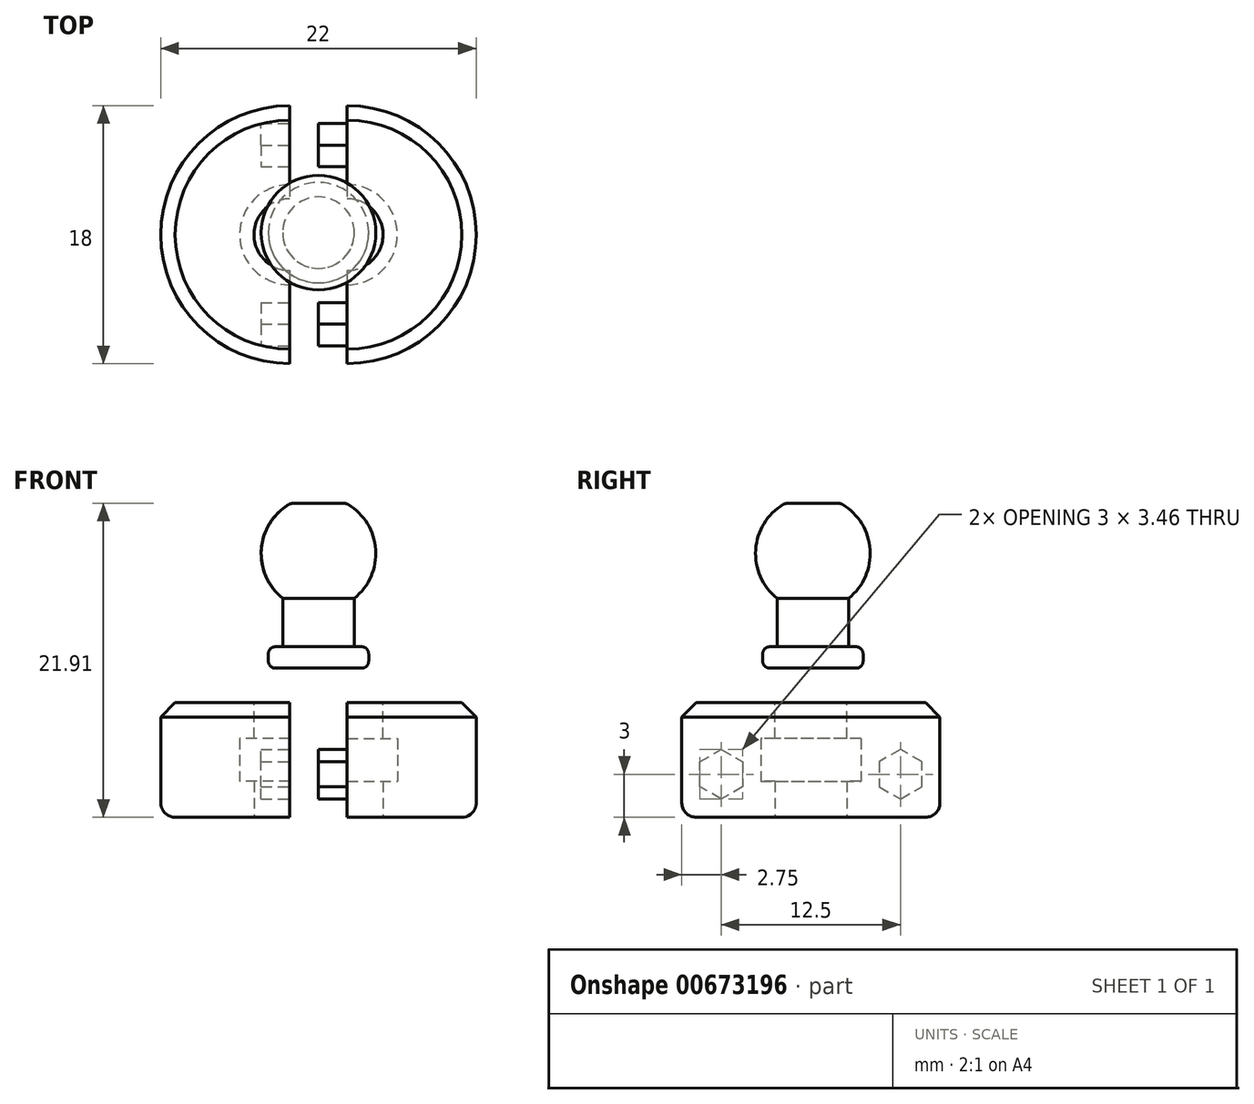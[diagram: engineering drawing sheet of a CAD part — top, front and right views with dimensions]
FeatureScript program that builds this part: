
annotation { "Feature Type Name" : "Feature", "Feature Type Description" : "" }
export const myFeature = defineFeature(function(context is Context, id is Id, definition is map)
    precondition{}
    {
        {
            var Q0;
            Q0=qCreatedBy(makeId("Right.planeOp"),FACE);
            var sketch = newSketch(context, id + "F0", { "sketchPlane" : qUnion([Q0])});
            skLineSegment(sketch, "E0.bottom", {"start": v(0, 0) * mm, "end": v(-18, 0) * mm});
            skLineSegment(sketch, "E0.top", {"start": v(0, 8) * mm, "end": v(-18, 8) * mm});
            skLineSegment(sketch, "E0.left", {"start": v(0, 0) * mm, "end": v(0, 8) * mm});
            skLineSegment(sketch, "E0.right", {"start": v(-18, 0) * mm, "end": v(-18, 8) * mm});
            skSolve(sketch);
        }
        {
            var Q0;
            Q0=makeQuery(id+"F0.imprint","IMPRINT",FACE,{"disambiguationData":[TD([[makeQuery(id+"F0.imprint","IMPRINT",EDGE,{"derivedFrom":sQuery(id+"F0.wireOp",EDGE,"E0.bottom")}),-1.0]])]});
            extrude(context, id + "F1", {"entities" : qUnion([Q0]), "depth" : 9 * mm});
        }
        {
            var Q0;
            Q0=makeQuery(id+"F1.opExtrude","SWEPT_FACE",FACE,{"disambiguationData":[OSD([sQuery(id+"F0.wireOp",EDGE,"E0.bottom")])]});
            var sketch = newSketch(context, id + "F2", { "sketchPlane" : qUnion([Q0])});
            skArc(sketch, "E1", {"start": v(9, 11.5) * mm, "mid": v(6.5, 9) * mm, "end": v(9, 6.5) * mm});
            skArc(sketch, "E2", {"start": v(9, 12.5) * mm, "mid": v(5.5, 9) * mm, "end": v(9, 5.5) * mm});
            skLineSegment(sketch, "E3", {"start": v(9, 12.5) * mm, "end": v(9, 5.5) * mm});
            skSolve(sketch);
        }
        {
            var Q0;
            Q0=qSketchRegion(id+"F2",true);
            extrude(context, id + "F3", {"entities" : qUnion([Q0]), "operationType" : NewBodyOperationType.REMOVE, "oppositeDirection" : true, "depth" : 4 * mm});
        }
        {
            var Q0;
            {var subQ0=sQuery(id+"F2.wireOp",EDGE,"E1");Q0=makeQuery(id+"F2.imprint","IMPRINT",FACE,{"disambiguationData":[TD([[makeQuery(id+"F2.imprint","IMPRINT",EDGE,{"derivedFrom":subQ0}),-1.0]])]});}
            extrude(context, id + "F4", {"entities" : qUnion([Q0]), "operationType" : NewBodyOperationType.ADD, "oppositeDirection" : true, "depth" : 2.5 * mm});
        }
        {
            var Q0;
            {var subQ0=sQuery(id+"F2.wireOp",EDGE,"E3");var subQ1=sQuery(id+"F2.wireOp",EDGE,"E1");var subQ3=sQuery(id+"F0.wireOp",EDGE,"E0.bottom");Q0=makeQuery(id+"F4.boolean.opBoolean","MERGE",FACE,{"derivedFrom":[makeQuery(id+"F1.opExtrude","CAP_FACE",FACE,{"disambiguationData":[OSD([subQ3,sQuery(id+"F0.wireOp",EDGE,"E0.top"),sQuery(id+"F0.wireOp",EDGE,"E0.left"),sQuery(id+"F0.wireOp",EDGE,"E0.right")])],"isStart":false}),makeQuery(id+"F4.opExtrude","SWEPT_FACE",FACE,{"disambiguationData":[OSD([subQ0]),TDD([makeQuery(id+"F2.imprint","IMPRINT",EDGE,{"disambiguationData":[TD([[makeQuery(id+"F2.imprint","INTERSECT",VERTEX,{"disambiguationData":[OD(1.0)],"derivedFrom":[subQ1,subQ0]}),1.0]])],"derivedFrom":subQ0})])]}),makeQuery(id+"F4.opExtrude","SWEPT_FACE",FACE,{"disambiguationData":[OSD([subQ0]),TDD([makeQuery(id+"F2.imprint","IMPRINT",EDGE,{"disambiguationData":[TD([[makeQuery(id+"F2.imprint","INTERSECT",VERTEX,{"disambiguationData":[OD(0.0)],"derivedFrom":[subQ1,subQ0]}),-1.0]])],"derivedFrom":subQ0})])]})]});}
            var sketch = newSketch(context, id + "F5", { "sketchPlane" : qUnion([Q0])});
            skSolve(sketch);
        }
        {
            var Q0;
            Q0=makeQuery(id+"F1.opExtrude","CAP_EDGE",EDGE,{"disambiguationData":[OSD([sQuery(id+"F0.wireOp",EDGE,"E0.right")])],"isStart":true});
            var Q1;
            Q1=makeQuery(id+"F1.opExtrude","CAP_EDGE",EDGE,{"disambiguationData":[OSD([sQuery(id+"F0.wireOp",EDGE,"E0.left")])],"isStart":true});
            fillet(context, id + "F6", {"entities" : qUnion([Q0, Q1]), "radius" : 9 * mm, "tangentPropagation" : true, "allowEdgeOverflow" : false});
        }
        {
            var Q0;
            {var subQ12=sQuery(id+"F0.wireOp",EDGE,"E0.top");Q0=makeQuery(id+"F5.imprint","IMPRINT",FACE,{"disambiguationData":[TD([[makeQuery(id+"F5.imprint","IMPRINT",EDGE,{"derivedFrom":makeQuery(id+"F1.opExtrude","CAP_EDGE",EDGE,{"disambiguationData":[OSD([subQ12])],"isStart":false})}),1.0]])]});}
            var sketch = newSketch(context, id + "F7", { "sketchPlane" : qUnion([Q0])});
            skLineSegment(sketch, "E4", {"start": v(0, 0) * mm, "end": v(-18, 0) * mm, "construction": true});
            skLineSegment(sketch, "E5", {"start": v(-9, 0) * mm, "end": v(-9, 6) * mm, "construction": true});
            skLineSegment(sketch, "E6", {"start": v(-9, 6) * mm, "end": v(-12.5, 6) * mm, "construction": true});
            skLineSegment(sketch, "E7.bottom", {"start": v(-12.5, 6) * mm, "end": v(-18, 6) * mm, "construction": true});
            skLineSegment(sketch, "E7.top", {"start": v(-12.5, 0) * mm, "end": v(-18, 0) * mm, "construction": true});
            skLineSegment(sketch, "E7.left", {"start": v(-12.5, 6) * mm, "end": v(-12.5, 0) * mm, "construction": true});
            skLineSegment(sketch, "E7.right", {"start": v(-18, 6) * mm, "end": v(-18, 0) * mm, "construction": true});
            skCircle(sketch, "E8.cCircle", {"center": v(-15.25, 3) * mm, "radius": 1.5 * mm});
            skPoint(sketch, "E8.cCircle.centerSnap0", {"position": v(-18, 3) * mm});
            skPoint(sketch, "E8.cCircle.centerSnap1", {"position": v(-15.25, 6) * mm});
            skLineSegment(sketch, "E8.0", {"start": v(-16.75, 2.13) * mm, "end": v(-16.75, 3.87) * mm});
            skLineSegment(sketch, "E8.1", {"start": v(-16.75, 3.87) * mm, "end": v(-15.25, 4.73) * mm});
            skLineSegment(sketch, "E8.2", {"start": v(-15.25, 4.73) * mm, "end": v(-13.75, 3.87) * mm});
            skLineSegment(sketch, "E8.3", {"start": v(-13.75, 3.87) * mm, "end": v(-13.75, 2.13) * mm});
            skLineSegment(sketch, "E8.4", {"start": v(-13.75, 2.13) * mm, "end": v(-15.25, 1.27) * mm});
            skLineSegment(sketch, "E8.5", {"start": v(-15.25, 1.27) * mm, "end": v(-16.75, 2.13) * mm});
            skPoint(sketch, "E8.0.midPoint", {"position": v(-16.75, 3) * mm});
            skLineSegment(sketch, "E9.MirrorCS", {"start": v(-2.75, 1.27) * mm, "end": v(-1.25, 2.13) * mm});
            skPoint(sketch, "E10.MirrorP", {"position": v(-1.25, 3) * mm});
            skLineSegment(sketch, "E11.MirrorCS", {"start": v(-4.25, 2.13) * mm, "end": v(-2.75, 1.27) * mm});
            skLineSegment(sketch, "E12.MirrorCS", {"start": v(-4.25, 3.87) * mm, "end": v(-4.25, 2.13) * mm});
            skLineSegment(sketch, "E13.MirrorCS", {"start": v(-2.75, 4.73) * mm, "end": v(-4.25, 3.87) * mm});
            skLineSegment(sketch, "E14.MirrorCS", {"start": v(-1.25, 2.13) * mm, "end": v(-1.25, 3.87) * mm});
            skLineSegment(sketch, "E15.MirrorCS", {"start": v(-1.25, 3.87) * mm, "end": v(-2.75, 4.73) * mm});
            skCircle(sketch, "E16.MirrorC", {"center": v(-2.75, 3) * mm, "radius": 1.5 * mm});
            skSolve(sketch);
        }
        {
            var Q0;
            Q0=qSketchRegion(id+"F7",true);
            extrude(context, id + "F8", {"entities" : qUnion([Q0]), "operationType" : NewBodyOperationType.REMOVE, "oppositeDirection" : true, "depth" : 2 * mm});
        }
        {
            var Q0;
            Q0=makeQuery(id+"F1.opExtrude","SWEPT_FACE",FACE,{"disambiguationData":[OSD([sQuery(id+"F0.wireOp",EDGE,"E0.top")])]});
            var sketch = newSketch(context, id + "F9", { "sketchPlane" : qUnion([Q0])});
            skArc(sketch, "E17", {"start": v(9, -6.5) * mm, "mid": v(6.5, -9) * mm, "end": v(9, -11.5) * mm});
            skArc(sketch, "E18", {"start": v(9, -5.5) * mm, "mid": v(5.5, -9) * mm, "end": v(9, -12.5) * mm});
            skLineSegment(sketch, "E19", {"start": v(9, -12.5) * mm, "end": v(9, -5.5) * mm});
            skSolve(sketch);
        }
        {
            var Q0;
            Q0=qSketchRegion(id+"F9",true);
            extrude(context, id + "F10", {"entities" : qUnion([Q0]), "operationType" : NewBodyOperationType.REMOVE, "oppositeDirection" : true, "depth" : 4 * mm});
        }
        {
            var Q0;
            {var subQ0=sQuery(id+"F9.wireOp",EDGE,"E17");Q0=makeQuery(id+"F9.imprint","IMPRINT",FACE,{"disambiguationData":[TD([[makeQuery(id+"F9.imprint","IMPRINT",EDGE,{"derivedFrom":subQ0}),-1.0]])]});}
            extrude(context, id + "F11", {"entities" : qUnion([Q0]), "operationType" : NewBodyOperationType.ADD, "oppositeDirection" : true, "depth" : 2.5 * mm});
        }
        {
            var Q0;
            Q0=qCreatedBy(makeId("Right.planeOp"),FACE);
            cPlane(context, id + "F12", {"entities" : qUnion([Q0]), "cplaneType" : CPlaneType.OFFSET, "offset" : 11 * mm, "width" : 150 * mm, "height" : 150 * mm});
        }
        {
            var Q0;
            Q0=qCreatedBy(id+"F12.planeOp",FACE);
            var sketch = newSketch(context, id + "F13", { "sketchPlane" : qUnion([Q0])});
            skLineSegment(sketch, "E20", {"start": v(-8.86, 10.4) * mm, "end": v(-8.86, 18.4) * mm, "construction": true});
            skLineSegment(sketch, "E21", {"start": v(-8.86, 10.4) * mm, "end": v(-12.36, 10.4) * mm});
            skLineSegment(sketch, "E22", {"start": v(-12.36, 10.4) * mm, "end": v(-12.36, 11.9) * mm});
            skLineSegment(sketch, "E23", {"start": v(-12.36, 11.9) * mm, "end": v(-11.36, 11.9) * mm});
            skLineSegment(sketch, "E24", {"start": v(-11.36, 11.9) * mm, "end": v(-11.36, 14.4) * mm});
            skLineSegment(sketch, "E25", {"start": v(-11.36, 14.4) * mm, "end": v(-8.86, 14.4) * mm, "construction": true});
            skArc(sketch, "E26", {"start": v(-10.8, 21.9) * mm, "mid": v(-12.85, 18.74) * mm, "end": v(-11.36, 15.28) * mm});
            skLineSegment(sketch, "E27", {"start": v(-11.36, 14.4) * mm, "end": v(-11.36, 15.28) * mm});
            skLineSegment(sketch, "E28", {"start": v(-8.86, 18.4) * mm, "end": v(-8.86, 22.4) * mm, "construction": true});
            skLineSegment(sketch, "E29", {"start": v(-8.86, 22.4) * mm, "end": v(-8.86, 21.9) * mm, "construction": true});
            skLineSegment(sketch, "E30", {"start": v(-8.86, 21.9) * mm, "end": v(-10.8, 21.9) * mm});
            skLineSegment(sketch, "E31", {"start": v(-8.86, 21.9) * mm, "end": v(-8.86, 10.4) * mm});
            skSolve(sketch);
        }
        {
            var Q0;
            Q0=qSketchRegion(id+"F13",true);
            var Q1;
            Q1=sQuery(id+"F13.wireOp",EDGE,"E31");
            revolve(context, id + "F14", {"entities" : qUnion([Q0]), "axis" : qUnion([Q1]), "revolveType" : RevolveType.FULL});
        }
        {
            var Q0;
            Q0=makeQuery(id+"F14.opRevolve","SWEPT_FACE",FACE,{"disambiguationData":[OSD([sQuery(id+"F13.wireOp",EDGE,"E22")])]});
            var Q1;
            Q1=makeQuery(id+"F14.opRevolve","SWEPT_EDGE",EDGE,{"disambiguationData":[OSD([sQuery(id+"F13.wireOp",EDGE,"E26"),sQuery(id+"F13.wireOp",EDGE,"E30")])]});
            fillet(context, id + "F15", {"entities" : qUnion([Q0, Q1]), "radius" : .5 * mm, "tangentPropagation" : true, "allowEdgeOverflow" : false});
        }
        {
            var Q0;
            Q0=makeQuery(id+"F1.opExtrude","SWEPT_BODY",BODY,{"disambiguationData":[OSD([sQuery(id+"F0.wireOp",EDGE,"E0.bottom"),sQuery(id+"F0.wireOp",EDGE,"E0.top"),sQuery(id+"F0.wireOp",EDGE,"E0.left"),sQuery(id+"F0.wireOp",EDGE,"E0.right")])]});
            var Q1;
            Q1=qCreatedBy(id+"F12.planeOp",FACE);
            mirror(context, id + "F16", {"entities" : qUnion([Q0]), "mirrorPlane" : qUnion([Q1])});
        }
        {
            var Q0;
            Q0=makeQuery(id+"F16.opPattern","COPY",FACE,{"derivedFrom":makeQuery(id+"F8.boolean.opBoolean","COPY",FACE,{"derivedFrom":makeQuery(id+"F8.opExtrude","CAP_FACE",FACE,{"disambiguationData":[OSD([sQuery(id+"F7.wireOp",EDGE,"E8.0"),sQuery(id+"F7.wireOp",EDGE,"E8.1"),sQuery(id+"F7.wireOp",EDGE,"E8.2"),sQuery(id+"F7.wireOp",EDGE,"E8.3"),sQuery(id+"F7.wireOp",EDGE,"E8.4"),sQuery(id+"F7.wireOp",EDGE,"E8.5")])],"isStart":false})}),"instanceName":"1"});
            var Q1;
            Q1=makeQuery(id+"F16.opPattern","COPY",FACE,{"derivedFrom":makeQuery(id+"F8.boolean.opBoolean","COPY",FACE,{"derivedFrom":makeQuery(id+"F8.opExtrude","CAP_FACE",FACE,{"disambiguationData":[OSD([sQuery(id+"F7.wireOp",EDGE,"E9.MirrorCS"),sQuery(id+"F7.wireOp",EDGE,"E11.MirrorCS"),sQuery(id+"F7.wireOp",EDGE,"E12.MirrorCS"),sQuery(id+"F7.wireOp",EDGE,"E13.MirrorCS"),sQuery(id+"F7.wireOp",EDGE,"E14.MirrorCS"),sQuery(id+"F7.wireOp",EDGE,"E15.MirrorCS")])],"isStart":false})}),"instanceName":"1"});
            extrude(context, id + "F17", {"entities" : qUnion([Q0, Q1]), "operationType" : NewBodyOperationType.ADD, "depth" : 4 * mm});
        }
        {
            var Q0;
            Q0=makeQuery(id+"F6.opFillet","BLEND_EDGE",EDGE,{"blendedFrom":[makeQuery(id+"F1.opExtrude","CAP_EDGE",EDGE,{"disambiguationData":[OSD([sQuery(id+"F0.wireOp",EDGE,"E0.left")])],"isStart":true}),makeQuery(id+"F4.boolean.opBoolean","MERGE",FACE,{"derivedFrom":[makeQuery(id+"F1.opExtrude","SWEPT_FACE",FACE,{"disambiguationData":[OSD([sQuery(id+"F0.wireOp",EDGE,"E0.bottom")])]}),makeQuery(id+"F4.opExtrude","CAP_FACE",FACE,{"disambiguationData":[OSD([sQuery(id+"F2.wireOp",EDGE,"E1"),sQuery(id+"F2.wireOp",EDGE,"E2"),sQuery(id+"F2.wireOp",EDGE,"E3")])],"isStart":true})]})],"blendedInto":[makeQuery(id+"F4.boolean.opBoolean","MERGE",FACE,{"derivedFrom":[makeQuery(id+"F1.opExtrude","SWEPT_FACE",FACE,{"disambiguationData":[OSD([sQuery(id+"F0.wireOp",EDGE,"E0.bottom")])]}),makeQuery(id+"F4.opExtrude","CAP_FACE",FACE,{"disambiguationData":[OSD([sQuery(id+"F2.wireOp",EDGE,"E1"),sQuery(id+"F2.wireOp",EDGE,"E2"),sQuery(id+"F2.wireOp",EDGE,"E3")])],"isStart":true})]})]});
            var Q1;
            Q1=makeQuery(id+"F16.opPattern","COPY",EDGE,{"derivedFrom":makeQuery(id+"F6.opFillet","BLEND_EDGE",EDGE,{"blendedFrom":[makeQuery(id+"F1.opExtrude","CAP_EDGE",EDGE,{"disambiguationData":[OSD([sQuery(id+"F0.wireOp",EDGE,"E0.left")])],"isStart":true}),makeQuery(id+"F4.boolean.opBoolean","MERGE",FACE,{"derivedFrom":[makeQuery(id+"F1.opExtrude","SWEPT_FACE",FACE,{"disambiguationData":[OSD([sQuery(id+"F0.wireOp",EDGE,"E0.bottom")])]}),makeQuery(id+"F4.opExtrude","CAP_FACE",FACE,{"disambiguationData":[OSD([sQuery(id+"F2.wireOp",EDGE,"E1"),sQuery(id+"F2.wireOp",EDGE,"E2"),sQuery(id+"F2.wireOp",EDGE,"E3")])],"isStart":true})]})],"blendedInto":[makeQuery(id+"F4.boolean.opBoolean","MERGE",FACE,{"derivedFrom":[makeQuery(id+"F1.opExtrude","SWEPT_FACE",FACE,{"disambiguationData":[OSD([sQuery(id+"F0.wireOp",EDGE,"E0.bottom")])]}),makeQuery(id+"F4.opExtrude","CAP_FACE",FACE,{"disambiguationData":[OSD([sQuery(id+"F2.wireOp",EDGE,"E1"),sQuery(id+"F2.wireOp",EDGE,"E2"),sQuery(id+"F2.wireOp",EDGE,"E3")])],"isStart":true})]})]}),"instanceName":"1"});
            fillet(context, id + "F18", {"entities" : qUnion([Q0, Q1]), "radius" : 1 * mm, "tangentPropagation" : true, "allowEdgeOverflow" : false});
        }
        {
            var Q0;
            Q0=makeQuery(id+"F6.opFillet","BLEND_EDGE",EDGE,{"blendedFrom":[makeQuery(id+"F1.opExtrude","CAP_EDGE",EDGE,{"disambiguationData":[OSD([sQuery(id+"F0.wireOp",EDGE,"E0.left")])],"isStart":true}),makeQuery(id+"F1.opExtrude","SWEPT_FACE",FACE,{"disambiguationData":[OSD([sQuery(id+"F0.wireOp",EDGE,"E0.top")])]})],"blendedInto":[makeQuery(id+"F1.opExtrude","SWEPT_FACE",FACE,{"disambiguationData":[OSD([sQuery(id+"F0.wireOp",EDGE,"E0.top")])]})]});
            var Q1;
            Q1=makeQuery(id+"F16.opPattern","COPY",EDGE,{"derivedFrom":makeQuery(id+"F6.opFillet","BLEND_EDGE",EDGE,{"blendedFrom":[makeQuery(id+"F1.opExtrude","CAP_EDGE",EDGE,{"disambiguationData":[OSD([sQuery(id+"F0.wireOp",EDGE,"E0.left")])],"isStart":true}),makeQuery(id+"F1.opExtrude","SWEPT_FACE",FACE,{"disambiguationData":[OSD([sQuery(id+"F0.wireOp",EDGE,"E0.top")])]})],"blendedInto":[makeQuery(id+"F1.opExtrude","SWEPT_FACE",FACE,{"disambiguationData":[OSD([sQuery(id+"F0.wireOp",EDGE,"E0.top")])]})]}),"instanceName":"1"});
            chamfer(context, id + "F19", {"entities" : qUnion([Q0, Q1]), "width" : 1 * mm, "tangentPropagation" : true});
        }
    });
